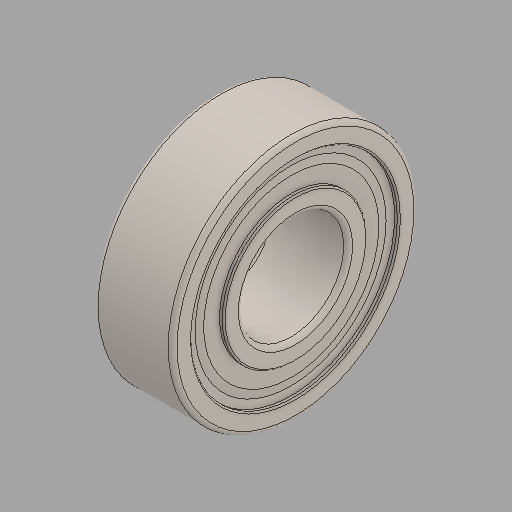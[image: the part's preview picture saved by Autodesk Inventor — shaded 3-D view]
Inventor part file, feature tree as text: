
AUTODESK INVENTOR PART (.ipt)
format: ipt  version: 2024.2 (Build 282272000, 272)  size: 243,200 bytes
history: native  units: in
note: dims shown in document units (in); Inventor stores cm internally (conversion verified against a paired STEP export)
features: revolve x1
ambient origin geometry x8: Origin, YZ Plane, XZ Plane, XY Plane, X Axis, Y Axis, Z Axis, Center Point
bodies: Solid1 (feature_tree)
feature tree (1):
  revolve  "Revolve1"  [1 undecoded]
note: 1 required parameter value undecoded (feature->parameter linkage not recoverable at this tier; creation-order binding heuristic only, values carry confidence <= 0.55)
